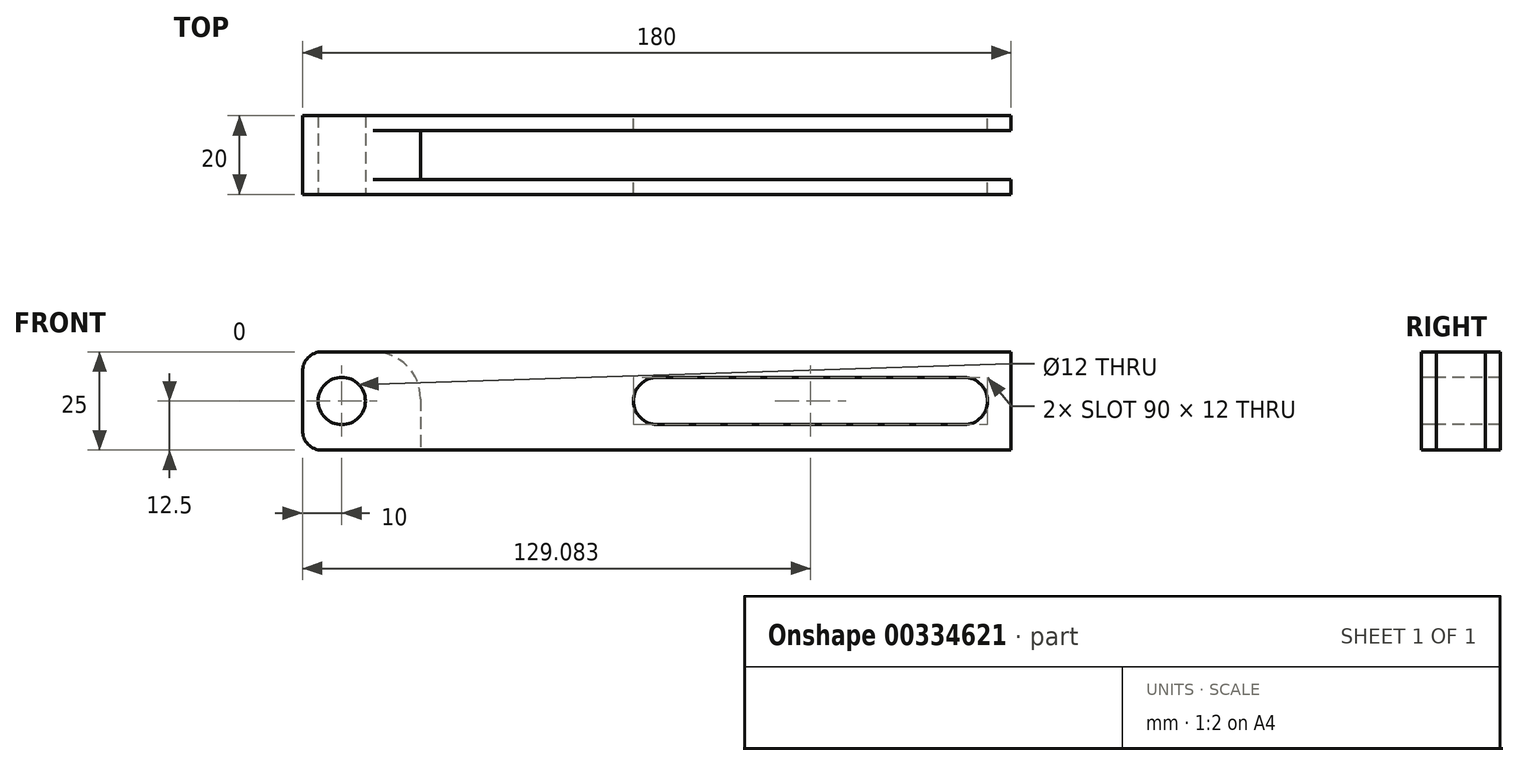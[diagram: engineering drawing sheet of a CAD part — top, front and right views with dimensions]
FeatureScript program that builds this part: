
annotation { "Feature Type Name" : "Feature", "Feature Type Description" : "" }
export const myFeature = defineFeature(function(context is Context, id is Id, definition is map)
    precondition{}
    {
        {
            var Q0;
            Q0=qCreatedBy(makeId("Front.planeOp"),FACE);
            var sketch = newSketch(context, id + "F0", { "sketchPlane" : qUnion([Q0])});
            skLineSegment(sketch, "E0.bottom", {"start": v(-90, 0) * mm, "end": v(90, 0) * mm});
            skLineSegment(sketch, "E0.top", {"start": v(-90, 25) * mm, "end": v(90, 25) * mm});
            skLineSegment(sketch, "E0.left", {"start": v(-90, 0) * mm, "end": v(-90, 25) * mm});
            skLineSegment(sketch, "E0.right", {"start": v(90, 0) * mm, "end": v(90, 25) * mm});
            skSolve(sketch);
        }
        {
            var Q0;
            Q0 = qSketchRegion(id + "F0", true);
            extrude(context, id + "F1", {"entities" : qUnion([Q0]), "endBound" : BoundingType.SYMMETRIC, "depth" : 20 * mm});
        }
        {
            var Q0;
            Q0=makeQuery(id+"F1.opExtrude","SWEPT_EDGE",EDGE,{"disambiguationData":[OSD([sQuery(id+"F0.wireOp",EDGE,"E0.top"),sQuery(id+"F0.wireOp",EDGE,"E0.left")])]});
            var Q1;
            Q1=makeQuery(id+"F1.opExtrude","SWEPT_EDGE",EDGE,{"disambiguationData":[OSD([sQuery(id+"F0.wireOp",EDGE,"E0.bottom"),sQuery(id+"F0.wireOp",EDGE,"E0.left")])]});
            fillet(context, id + "F2", {"entities" : qUnion([Q0, Q1]), "radius" : 5 * mm, "tangentPropagation" : true, "allowEdgeOverflow" : false});
        }
        {
            var Q0;
            Q0=qCreatedBy(makeId("Front.planeOp"),FACE);
            var sketch = newSketch(context, id + "F3", { "sketchPlane" : qUnion([Q0])});
            skCircle(sketch, "E1", {"center": v(-80, 12.5) * mm, "radius": 6 * mm});
            skSolve(sketch);
        }
        {
            var Q0;
            Q0 = qSketchRegion(id + "F3", true);
            extrude(context, id + "F4", {"entities" : qUnion([Q0]), "operationType" : NewBodyOperationType.REMOVE, "endBound" : BoundingType.SYMMETRIC, "oppositeDirection" : true, "depth" : 25 * mm});
        }
        {
            var Q0;
            Q0=qCreatedBy(makeId("Front.planeOp"),FACE);
            var sketch = newSketch(context, id + "F5", { "sketchPlane" : qUnion([Q0])});
            skLineSegment(sketch, "E2.bottom", {"start": v(-5.92, 18.5) * mm, "end": v(84.08, 18.5) * mm});
            skLineSegment(sketch, "E2.top", {"start": v(-5.92, 6.5) * mm, "end": v(84.08, 6.5) * mm});
            skLineSegment(sketch, "E2.left", {"start": v(-5.92, 18.5) * mm, "end": v(-5.92, 6.5) * mm});
            skLineSegment(sketch, "E2.right", {"start": v(84.08, 18.5) * mm, "end": v(84.08, 6.5) * mm});
            skSolve(sketch);
        }
        {
            var Q0;
            Q0 = qSketchRegion(id + "F5", true);
            extrude(context, id + "F6", {"entities" : qUnion([Q0]), "operationType" : NewBodyOperationType.REMOVE, "endBound" : BoundingType.SYMMETRIC, "oppositeDirection" : true, "depth" : 25 * mm});
        }
        {
            var Q0;
            Q0=makeQuery(id+"F6.boolean.opBoolean","COPY",EDGE,{"derivedFrom":makeQuery(id+"F6.opExtrude","SWEPT_EDGE",EDGE,{"disambiguationData":[OSD([sQuery(id+"F5.wireOp",EDGE,"E2.top"),sQuery(id+"F5.wireOp",EDGE,"E2.left")])]})});
            var Q1;
            Q1=makeQuery(id+"F6.boolean.opBoolean","COPY",EDGE,{"derivedFrom":makeQuery(id+"F6.opExtrude","SWEPT_EDGE",EDGE,{"disambiguationData":[OSD([sQuery(id+"F5.wireOp",EDGE,"E2.bottom"),sQuery(id+"F5.wireOp",EDGE,"E2.left")])]})});
            var Q2;
            Q2=makeQuery(id+"F6.boolean.opBoolean","COPY",EDGE,{"derivedFrom":makeQuery(id+"F6.opExtrude","SWEPT_EDGE",EDGE,{"disambiguationData":[OSD([sQuery(id+"F5.wireOp",EDGE,"E2.bottom"),sQuery(id+"F5.wireOp",EDGE,"E2.right")])]})});
            var Q3;
            Q3=makeQuery(id+"F6.boolean.opBoolean","COPY",EDGE,{"derivedFrom":makeQuery(id+"F6.opExtrude","SWEPT_EDGE",EDGE,{"disambiguationData":[OSD([sQuery(id+"F5.wireOp",EDGE,"E2.top"),sQuery(id+"F5.wireOp",EDGE,"E2.right")])]})});
            fillet(context, id + "F7", {"entities" : qUnion([Q0, Q1, Q2, Q3]), "radius" : 6 * mm, "tangentPropagation" : true, "allowEdgeOverflow" : false});
        }
        {
            var Q0;
            Q0=makeQuery(id+"F1.opExtrude","SWEPT_FACE",FACE,{"disambiguationData":[OSD([sQuery(id+"F0.wireOp",EDGE,"E0.right")])]});
            var sketch = newSketch(context, id + "F8", { "sketchPlane" : qUnion([Q0])});
            skLineSegment(sketch, "E3.bottom", {"start": v(-6.25, 26.67) * mm, "end": v(6.25, 26.67) * mm});
            skLineSegment(sketch, "E3.top", {"start": v(-6.25, 0) * mm, "end": v(6.25, 0) * mm});
            skLineSegment(sketch, "E3.left", {"start": v(-6.25, 26.67) * mm, "end": v(-6.25, 0) * mm});
            skLineSegment(sketch, "E3.right", {"start": v(6.25, 26.67) * mm, "end": v(6.25, 0) * mm});
            skSolve(sketch);
        }
        {
            var Q0;
            Q0 = qSketchRegion(id + "F8", true);
            extrude(context, id + "F9", {"entities" : qUnion([Q0]), "operationType" : NewBodyOperationType.REMOVE, "oppositeDirection" : true, "depth" : 150 * mm});
        }
        {
            var Q0;
            Q0=makeQuery(id+"F9.boolean.opBoolean","INTERSECT",EDGE,{"derivedFrom":[makeQuery(id+"F1.opExtrude","SWEPT_FACE",FACE,{"disambiguationData":[OSD([sQuery(id+"F0.wireOp",EDGE,"E0.top")])]}),makeQuery(id+"F9.opExtrude","CAP_FACE",FACE,{"disambiguationData":[OSD([sQuery(id+"F8.wireOp",EDGE,"E3.bottom"),sQuery(id+"F8.wireOp",EDGE,"E3.top"),sQuery(id+"F8.wireOp",EDGE,"E3.left"),sQuery(id+"F8.wireOp",EDGE,"E3.right")])],"isStart":false})]});
            var Q1;
            Q1=makeQuery(id+"F9.boolean.opBoolean","COPY",EDGE,{"derivedFrom":makeQuery(id+"F9.opExtrude","CAP_EDGE",EDGE,{"disambiguationData":[OSD([sQuery(id+"F8.wireOp",EDGE,"E3.top")])],"isStart":false})});
            fillet(context, id + "F10", {"entities" : qUnion([Q0, Q1]), "radius" : 12 * mm, "tangentPropagation" : true, "allowEdgeOverflow" : false});
        }
    });
